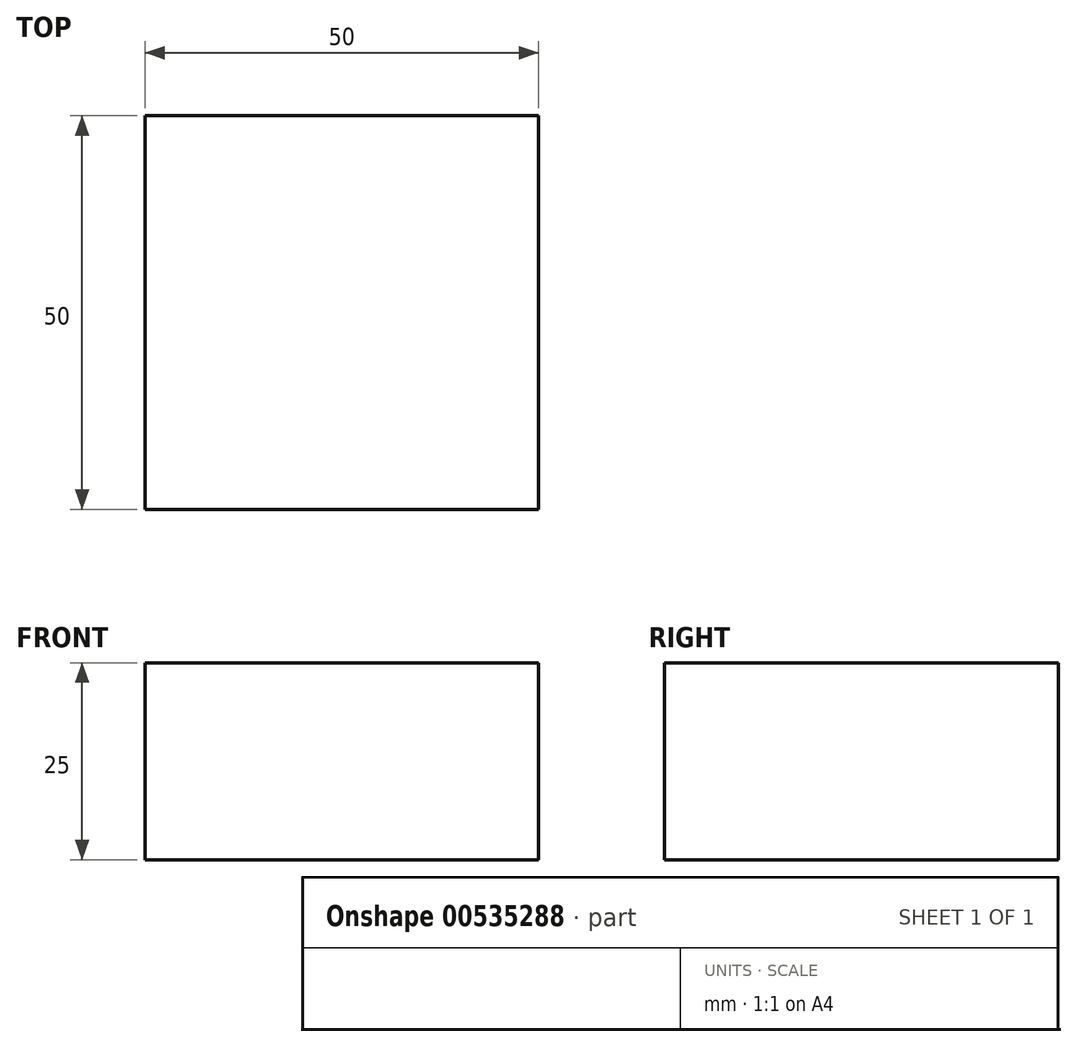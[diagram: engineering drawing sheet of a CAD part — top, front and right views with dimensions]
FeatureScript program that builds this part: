
annotation { "Feature Type Name" : "Feature", "Feature Type Description" : "" }
export const myFeature = defineFeature(function(context is Context, id is Id, definition is map)
    precondition{}
    {
        {
            var Q0;
            Q0=qCreatedBy(makeId("Top.planeOp"),FACE);
            var sketch = newSketch(context, id + "F0", { "sketchPlane" : qUnion([Q0])});
            skLineSegment(sketch, "E0.bottom", {"start": v(9.26, -18.31) * mm, "end": v(59.26, -18.31) * mm});
            skLineSegment(sketch, "E0.top", {"start": v(9.26, -68.31) * mm, "end": v(59.26, -68.31) * mm});
            skLineSegment(sketch, "E0.left", {"start": v(9.26, -18.31) * mm, "end": v(9.26, -68.31) * mm});
            skLineSegment(sketch, "E0.right", {"start": v(59.26, -18.31) * mm, "end": v(59.26, -68.31) * mm});
            skSolve(sketch);
        }
        {
            var Q0;
            Q0 = qSketchRegion(id + "F0", true);
            extrude(context, id + "F1", {"entities" : qUnion([Q0]), "depth" : 25 * mm, "offsetDistance" : 25 * mm});
        }
    });
